# Revit family: Drinking_Fountain-Oasis-Aqua_Pointe_Sports_Bottle_Filler-MG8SBF
name_source: partatom
category: Plumbing Fixtures
revit_build: Autodesk Revit MEP 2013 (Build: 20130531_2115(x64)
units: mm (PartAtom-declared; Revit-internal decimal feet)

## types (2) — shared parameters
Base Material = Metal - Oasis International - Brushed Stainless Steel - Exterior Finish
Chiller = Yes
Compression HP = 0 VA
Default Elevation = 2' - 3"
Description = Aqua Pointe Sports Bottle Filler
Finish = Metal - Oasis International - Brushed Stainless Steel - Exterior Finish
Full Load Amps = 5 A
Manufacturer = Oasis International
Manufacturer Fax Number = (614)322-4557
Metal Finish = Metal - Oasis International - Brushed Stainless Steel - Exterior Finish
Number of Poles = 1
Power Factor = 1
Product Documentation Link = http://www.oasiscoolers.com
Product Name = Radii Fountain w/ Sports Bottle Filler
Product Page URL = http://www.oasiscoolers.com
URL = http://www.oasiscoolers.com
Voltage = 115 V
Width = 3' - 2 3/4"

## per-type parameters (varying)
| type | Apparent Load | Base Rate | Rated Capacity | Rated Watts |
| MG8SBF | 550 VA | 8 GPM | 8 GPM | 550 W |
| MG12SBF | 620 VA | 12 GPM | 12 GPM | 620 W |

note: column(s) folded — value = type name in every type: Model

## geometry (parser evidence)
native form markers: Blend x4, Sweep x23
no freeform markers — native parametric forms only
